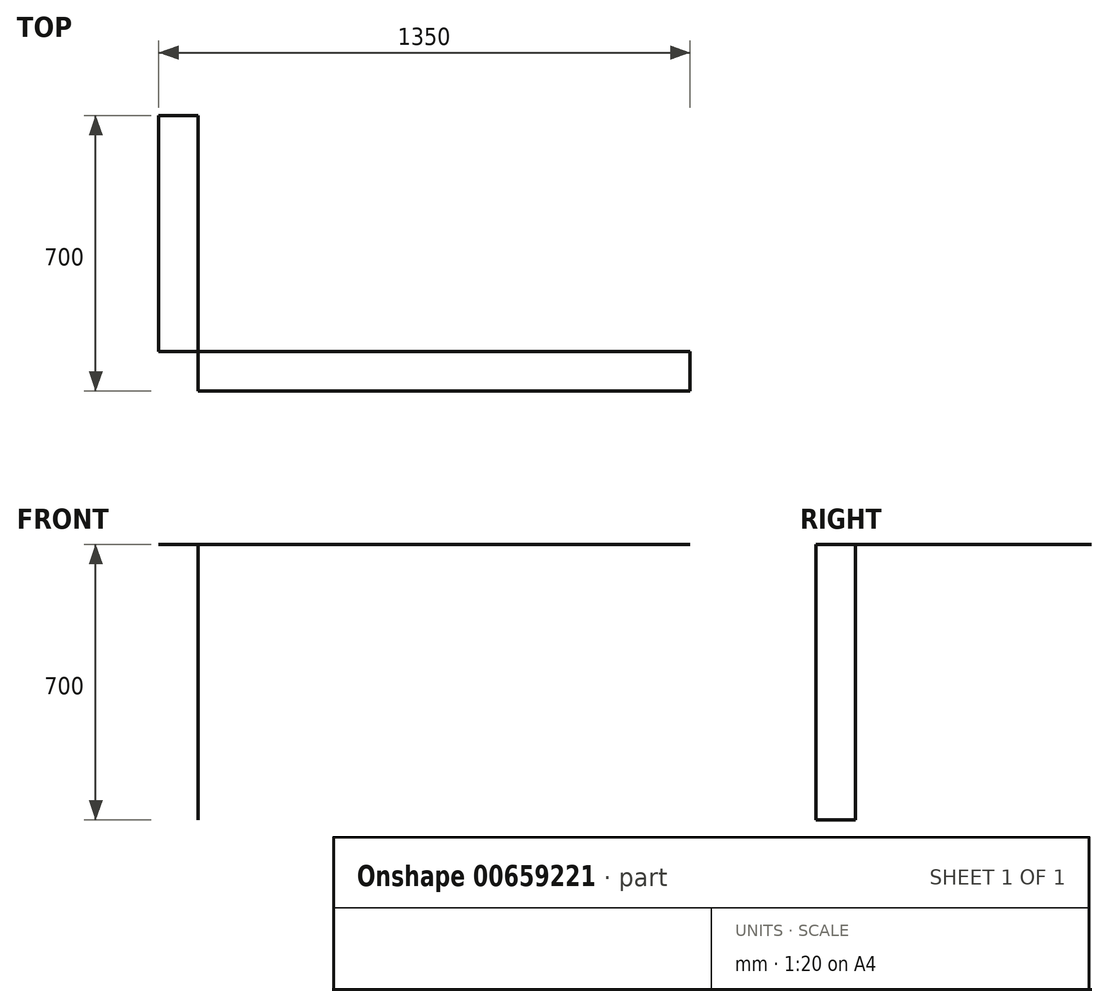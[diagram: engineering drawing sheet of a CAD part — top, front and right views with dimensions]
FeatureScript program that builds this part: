
annotation { "Feature Type Name" : "Feature", "Feature Type Description" : "" }
export const myFeature = defineFeature(function(context is Context, id is Id, definition is map)
    precondition{}
    {
        {
            var Q0;
            Q0=qCreatedBy(makeId("Front.planeOp"),FACE);
            var sketch = newSketch(context, id + "F0", { "sketchPlane" : qUnion([Q0])});
            skLineSegment(sketch, "E0", {"start": v(0, 0) * mm, "end": v(0, -350) * mm});
            skLineSegment(sketch, "E1", {"start": v(0, 0) * mm, "end": v(0, 350) * mm});
            skLineSegment(sketch, "E2", {"start": v(0, 350) * mm, "end": v(1250, 350) * mm});
            skSolve(sketch);
        }
        {
            var Q0;
            Q0=qCreatedBy(makeId("Right.planeOp"),FACE);
            var sketch = newSketch(context, id + "F1", { "sketchPlane" : qUnion([Q0])});
            skLineSegment(sketch, "E3", {"start": v(0, 350) * mm, "end": v(600, 350) * mm});
            skSolve(sketch);
        }
        {
            var Q0;
            Q0=sQuery(id+"F0.wireOp",EDGE,"E2");
            var Q1;
            Q1=sQuery(id+"F0.wireOp",EDGE,"E1");
            var Q2;
            Q2=sQuery(id+"F0.wireOp",EDGE,"E0");
            extrude(context, id + "F2", {"bodyType" : ToolBodyType.SURFACE, "surfaceEntities" : qUnion([Q0, Q1, Q2]), "depth" : 100 * mm, "offsetDistance" : 25 * mm});
        }
        {
            var Q0;
            Q0=sQuery(id+"F1.wireOp",EDGE,"E3");
            extrude(context, id + "F3", {"bodyType" : ToolBodyType.SURFACE, "surfaceEntities" : qUnion([Q0]), "oppositeDirection" : true, "depth" : 100 * mm, "offsetDistance" : 25 * mm});
        }
    });
